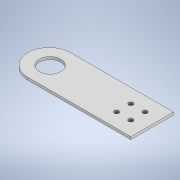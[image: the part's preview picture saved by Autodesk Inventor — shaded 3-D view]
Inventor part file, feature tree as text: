
AUTODESK INVENTOR PART (.ipt)
format: ipt  version: 2022 (Build 260153000, 153)  size: 129,536 bytes
history: native  units: mm
features: sheet_metal_op x1, fillet x1, sketch x1, other x1
ambient origin geometry x8: Origin, YZ Plane, XZ Plane, XY Plane, X Axis, Y Axis, Z Axis, Center Point
bodies: Body1 (feature_tree)
feature tree (4):
  sheet_metal_op  "Face2"
  fillet  "Fillet1"  Radius=24.0mm
  sketch  "Sketch1"  dims[d1=24.0mm d6=12.2mm d20=12.5mm d21=12.0mm d22=46.0mm d23=2.5mm d24=8.0mm d25=8.0mm d26=20.0mm d28=8.0mm d29=20.0mm d31=8.0mm d34=1.5mm d35=12.0mm]
  other  "Plate2"
